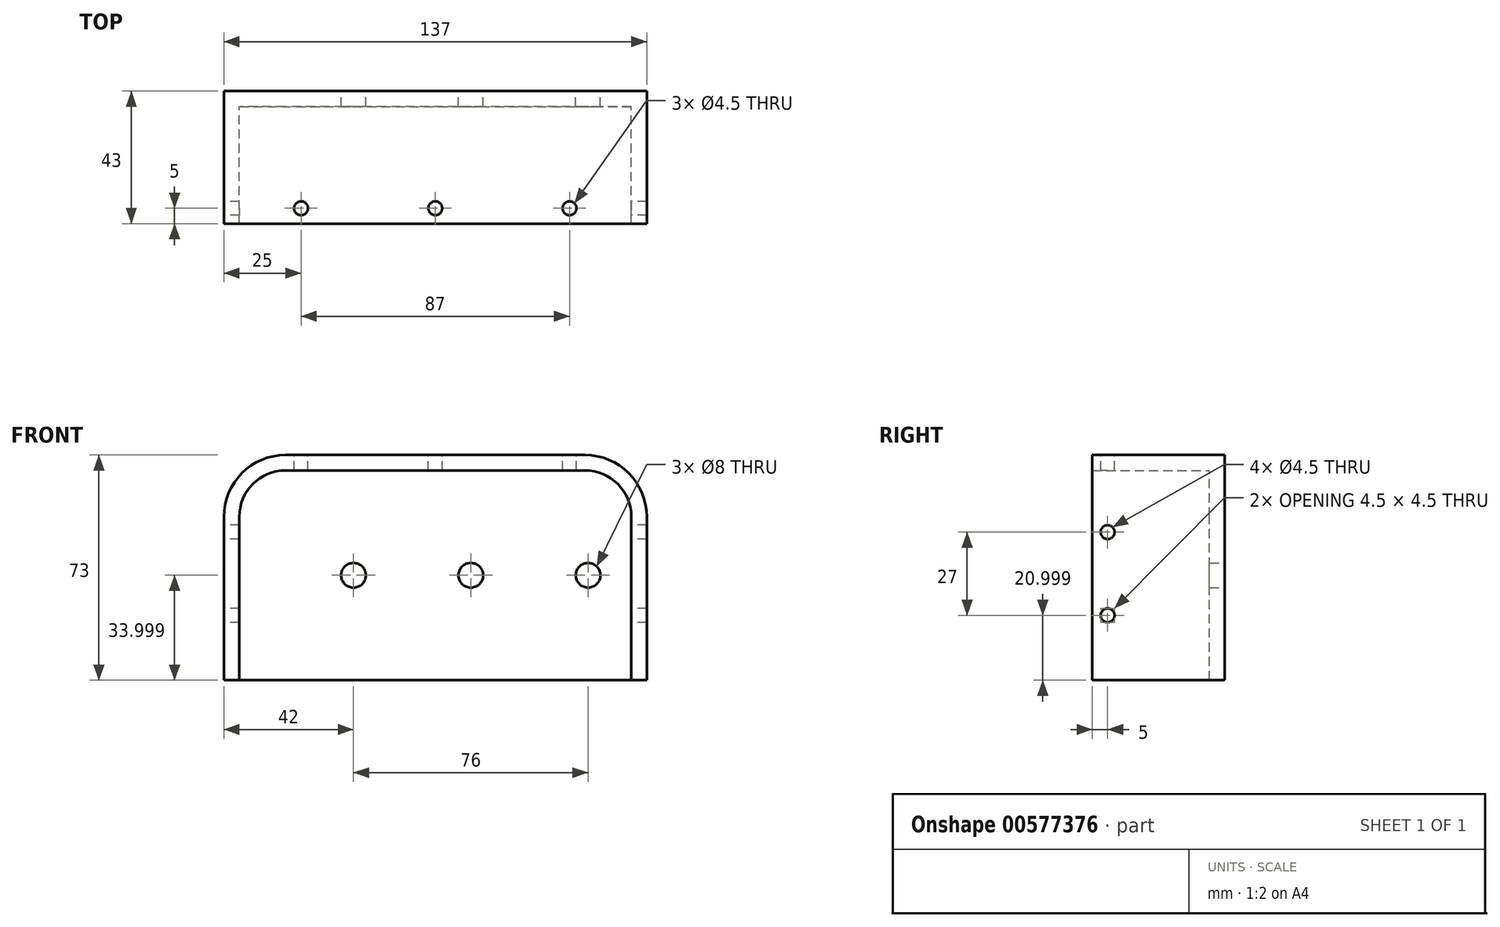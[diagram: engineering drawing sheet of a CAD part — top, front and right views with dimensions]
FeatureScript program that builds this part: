
annotation { "Feature Type Name" : "Feature", "Feature Type Description" : "" }
export const myFeature = defineFeature(function(context is Context, id is Id, definition is map)
    precondition{}
    {
        {
            var Q0;
            Q0=qCreatedBy(makeId("Front.planeOp"),FACE);
            var sketch = newSketch(context, id + "F0", { "sketchPlane" : qUnion([Q0])});
            skLineSegment(sketch, "E0.bottom", {"start": v(-80, 82.6) * mm, "end": v(57, 82.6) * mm});
            skLineSegment(sketch, "E0.top", {"start": v(-80, 9.6) * mm, "end": v(57, 9.6) * mm});
            skLineSegment(sketch, "E0.left", {"start": v(-80, 82.6) * mm, "end": v(-80, 9.6) * mm});
            skLineSegment(sketch, "E0.right", {"start": v(57, 82.6) * mm, "end": v(57, 9.6) * mm});
            skCircle(sketch, "E1", {"center": v(-38, 43.6) * mm, "radius": 4 * mm});
            skCircle(sketch, "E2", {"center": v(0, 43.6) * mm, "radius": 4 * mm});
            skCircle(sketch, "E3", {"center": v(38, 43.6) * mm, "radius": 4 * mm});
            skSolve(sketch);
        }
        {
            var Q0;
            Q0=makeQuery(id+"F0.imprint","IMPRINT",FACE,{"disambiguationData":[TD([[makeQuery(id+"F0.imprint","IMPRINT",EDGE,{"derivedFrom":sQuery(id+"F0.wireOp",EDGE,"E0.bottom")}),-1.0]])]});
            extrude(context, id + "F1", {"entities" : qUnion([Q0]), "depth" : 5 * mm, "offsetDistance" : 25 * mm});
        }
        {
            var Q0;
            Q0=makeQuery(id+"F1.opExtrude","CAP_FACE",FACE,{"disambiguationData":[OSD([sQuery(id+"F0.wireOp",EDGE,"E0.bottom"),sQuery(id+"F0.wireOp",EDGE,"E0.top"),sQuery(id+"F0.wireOp",EDGE,"E0.left"),sQuery(id+"F0.wireOp",EDGE,"E0.right"),sQuery(id+"F0.wireOp",EDGE,"E1"),sQuery(id+"F0.wireOp",EDGE,"E2"),sQuery(id+"F0.wireOp",EDGE,"E3")])],"isStart":false});
            var sketch = newSketch(context, id + "F2", { "sketchPlane" : qUnion([Q0])});
            skLineSegment(sketch, "E4", {"start": v(-80, 9.6) * mm, "end": v(-80, 82.6) * mm});
            skLineSegment(sketch, "E5", {"start": v(-80, 82.6) * mm, "end": v(57, 82.6) * mm});
            skLineSegment(sketch, "E6", {"start": v(57, 82.6) * mm, "end": v(57, 9.6) * mm});
            skLineSegment(sketch, "E7", {"start": v(57, 9.6) * mm, "end": v(52, 9.6) * mm});
            skLineSegment(sketch, "E8", {"start": v(52, 9.6) * mm, "end": v(52, 77.6) * mm});
            skLineSegment(sketch, "E9", {"start": v(52, 77.6) * mm, "end": v(-75, 77.6) * mm});
            skLineSegment(sketch, "E10", {"start": v(-75, 77.6) * mm, "end": v(-75, 34.58) * mm});
            skLineSegment(sketch, "E11", {"start": v(-75, 34.58) * mm, "end": v(-75, 9.6) * mm});
            skLineSegment(sketch, "E12", {"start": v(-75, 9.6) * mm, "end": v(-80, 9.6) * mm});
            skSolve(sketch);
        }
        {
            var Q0;
            Q0 = qSketchRegion(id + "F2", true);
            extrude(context, id + "F3", {"entities" : qUnion([Q0]), "operationType" : NewBodyOperationType.ADD, "depth" : (23 + 5 + 10) * mm, "offsetDistance" : 25 * mm});
        }
        {
            var Q0;
            Q0=makeQuery(id+"F3.boolean.opBoolean","MERGE",FACE,{"derivedFrom":[makeQuery(id+"F1.opExtrude","SWEPT_FACE",FACE,{"disambiguationData":[OSD([sQuery(id+"F0.wireOp",EDGE,"E0.left")])]}),makeQuery(id+"F3.opExtrude","SWEPT_FACE",FACE,{"disambiguationData":[OSD([sQuery(id+"F2.wireOp",EDGE,"E4")])]})]});
            var sketch = newSketch(context, id + "F4", { "sketchPlane" : qUnion([Q0])});
            skSolve(sketch);
        }
        {
            var Q0;
            {var subQ0=sQuery(id+"F0.wireOp",EDGE,"E0.left");Q0=makeQuery(id+"F4.imprint","IMPRINT",FACE,{"disambiguationData":[TD([[makeQuery(id+"F4.imprint","IMPRINT",EDGE,{"derivedFrom":makeQuery(id+"F1.opExtrude","CAP_EDGE",EDGE,{"disambiguationData":[OSD([subQ0])],"isStart":true})}),1.0]])]});}
            var sketch = newSketch(context, id + "F5", { "sketchPlane" : qUnion([Q0])});
            skCircle(sketch, "E13", {"center": v(38, 57.6) * mm, "radius": 2.25 * mm});
            skCircle(sketch, "E14", {"center": v(38, 30.6) * mm, "radius": 2.25 * mm});
            skSolve(sketch);
        }
        {
            var Q0;
            Q0 = qSketchRegion(id + "F5", true);
            extrude(context, id + "F6", {"entities" : qUnion([Q0]), "operationType" : NewBodyOperationType.REMOVE, "endBound" : BoundingType.THROUGH_ALL, "oppositeDirection" : true, "depth" : 25 * mm, "offsetDistance" : 25 * mm});
        }
        {
            var Q0;
            Q0=makeQuery(id+"F3.boolean.opBoolean","MERGE",FACE,{"derivedFrom":[makeQuery(id+"F1.opExtrude","SWEPT_FACE",FACE,{"disambiguationData":[OSD([sQuery(id+"F0.wireOp",EDGE,"E0.bottom")])]}),makeQuery(id+"F3.opExtrude","SWEPT_FACE",FACE,{"disambiguationData":[OSD([sQuery(id+"F2.wireOp",EDGE,"E5")])]})]});
            var sketch = newSketch(context, id + "F7", { "sketchPlane" : qUnion([Q0])});
            skCircle(sketch, "E15", {"center": v(-55, -38) * mm, "radius": 2.25 * mm});
            skCircle(sketch, "E16", {"center": v(-11.5, -38) * mm, "radius": 2.25 * mm});
            skCircle(sketch, "E17", {"center": v(32, -38) * mm, "radius": 2.25 * mm});
            skSolve(sketch);
        }
        {
            var Q0;
            Q0 = qSketchRegion(id + "F7", true);
            extrude(context, id + "F8", {"entities" : qUnion([Q0]), "operationType" : NewBodyOperationType.REMOVE, "endBound" : BoundingType.UP_TO_NEXT, "oppositeDirection" : true, "depth" : 25 * mm, "offsetDistance" : 25 * mm});
        }
        {
            var Q0;
            Q0=makeQuery(id+"F3.opExtrude","SWEPT_EDGE",EDGE,{"disambiguationData":[OSD([sQuery(id+"F2.wireOp",EDGE,"E9"),sQuery(id+"F2.wireOp",EDGE,"E10")])]});
            var Q1;
            Q1=makeQuery(id+"F3.opExtrude","SWEPT_EDGE",EDGE,{"disambiguationData":[OSD([sQuery(id+"F2.wireOp",EDGE,"E8"),sQuery(id+"F2.wireOp",EDGE,"E9")])]});
            fillet(context, id + "F9", {"entities" : qUnion([Q0, Q1]), "radius" : 15 * mm, "tangentPropagation" : true, "allowEdgeOverflow" : false});
        }
        {
            var Q0;
            Q0=makeQuery(id+"F3.boolean.opBoolean","MERGE",EDGE,{"derivedFrom":[makeQuery(id+"F1.opExtrude","SWEPT_EDGE",EDGE,{"disambiguationData":[OSD([sQuery(id+"F0.wireOp",EDGE,"E0.bottom"),sQuery(id+"F0.wireOp",EDGE,"E0.left")])]}),makeQuery(id+"F3.opExtrude","SWEPT_EDGE",EDGE,{"disambiguationData":[OSD([sQuery(id+"F2.wireOp",EDGE,"E4"),sQuery(id+"F2.wireOp",EDGE,"E5")])]})]});
            var Q1;
            Q1=makeQuery(id+"F3.boolean.opBoolean","MERGE",EDGE,{"derivedFrom":[makeQuery(id+"F1.opExtrude","SWEPT_EDGE",EDGE,{"disambiguationData":[OSD([sQuery(id+"F0.wireOp",EDGE,"E0.bottom"),sQuery(id+"F0.wireOp",EDGE,"E0.right")])]}),makeQuery(id+"F3.opExtrude","SWEPT_EDGE",EDGE,{"disambiguationData":[OSD([sQuery(id+"F2.wireOp",EDGE,"E5"),sQuery(id+"F2.wireOp",EDGE,"E6")])]})]});
            fillet(context, id + "F10", {"entities" : qUnion([Q0, Q1]), "radius" : 20 * mm, "tangentPropagation" : true, "allowEdgeOverflow" : false});
        }
    });
